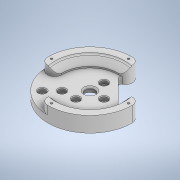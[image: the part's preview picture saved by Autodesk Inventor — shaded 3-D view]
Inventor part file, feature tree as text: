
AUTODESK INVENTOR PART (.ipt)
format: ipt  version: 2021 (Build 250183000, 183)  size: 337,408 bytes
history: native  units: mm
features: extrude x11, sketch x11, fillet x3, chamfer x3
ambient origin geometry x8: Origin, YZ Plane, XZ Plane, XY Plane, X Axis, Y Axis, Z Axis, Center Point
bodies: Solid1 (feature_tree)
feature tree (28):
  extrude  "Extrusion1"  Depth=10.0mm TaperAngle=0.0deg
  extrude  "Extrusion2"  Depth=10.0mm TaperAngle=0.0deg
  extrude  "Extrusion3"  Depth=2.0mm TaperAngle=0.0deg
  fillet  "Fillet1"  Radius=2.0mm
  chamfer  "Chamfer1"  Distance=8.0mm Angle=45.0deg
  extrude  "Extrusion4"  Depth=3.1mm
  extrude  "Extrusion5"  Depth=3.1mm
  extrude  "Extrusion6"  TaperAngle=0.0deg  [1 undecoded]
  fillet  "Fillet2"  [1 undecoded]
  extrude  "Extrusion7"  Depth=55.0mm
  extrude  "Extrusion8"  Depth=55.0mm
  chamfer  "Chamfer2"  Distance=2.0mm
  extrude  "Extrusion9"  Depth=5.5mm
  extrude  "Extrusion10"  Depth=5.5mm
  fillet  "Fillet3"  Radius=5.0mm
  extrude  "Extrusion11"  Depth=2.0mm
  chamfer  "Chamfer3"  Distance=25.0mm
  sketch  "Sketch1"  dims[d0=120.0mm d1=10.0mm d2=0.0mm]
  sketch  "Sketch2"  dims[d3=80.0mm d4=10.0mm d5=0.0mm]
  sketch  "Sketch3"  dims[d6=100.0mm d7=2.0mm d8=0.0mm d9=2.0mm d10=8.0mm d11=2.0mm d12=45.0deg]
  sketch  "Sketch4"  dims[d13=3.1mm d14=3.1mm]
  sketch  "Sketch5"  dims[d15=3.1mm d16=3.1mm]
  sketch  "Sketch6"  dims[d17=0.0mm d18=0.0mm d19=0.0mm]
  sketch  "Sketch7"  dims[d20=55.0mm d21=55.0mm]
  sketch  "Sketch8"  dims[d22=55.0mm d23=55.0mm]
  sketch  "Sketch10"  dims[d24=0.0mm d25=2.0mm d26=0.0mm]
  sketch  "Sketch12"  dims[d27=5.5mm d28=5.5mm]
  sketch  "Sketch13"  dims[d29=5.5mm d30=5.5mm d31=5.0mm d32=0.0mm d33=25.0mm d34=25.0mm d35=45.0deg d36=25.0mm d37=0.0mm d38=10.0mm d39=22.4mm d40=7.0mm d41=0.0mm d42=14.0mm d43=7.0mm d44=0.0mm d45=2.0mm d46=2.0mm d47=45.0deg d48=4.1mm d49=4.1mm d50=4.1mm d51=4.1mm d52=0.0mm d53=0.0mm d54=0.0mm d55=0.0mm d56=40.0mm d57=20.0mm d58=40.0mm d59=20.0mm d60=7.0mm d61=0.0mm d62=4.1mm d63=20.0mm d64=20.0mm d65=4.1mm d66=20.0mm d67=10.0mm d68=10.0mm d69=10.0mm d70=60.0mm d71=7.0mm d72=0.0mm d73=3.0mm d74=10.0mm d75=10.0mm d76=10.0mm d77=10.0mm d78=10.0mm d79=5.0mm d80=0.0mm d81=1.0mm d82=2.0mm d83=45.0deg]
note: 2 required parameter values undecoded (feature->parameter linkage not recoverable at this tier; creation-order binding heuristic only, values carry confidence <= 0.55)
